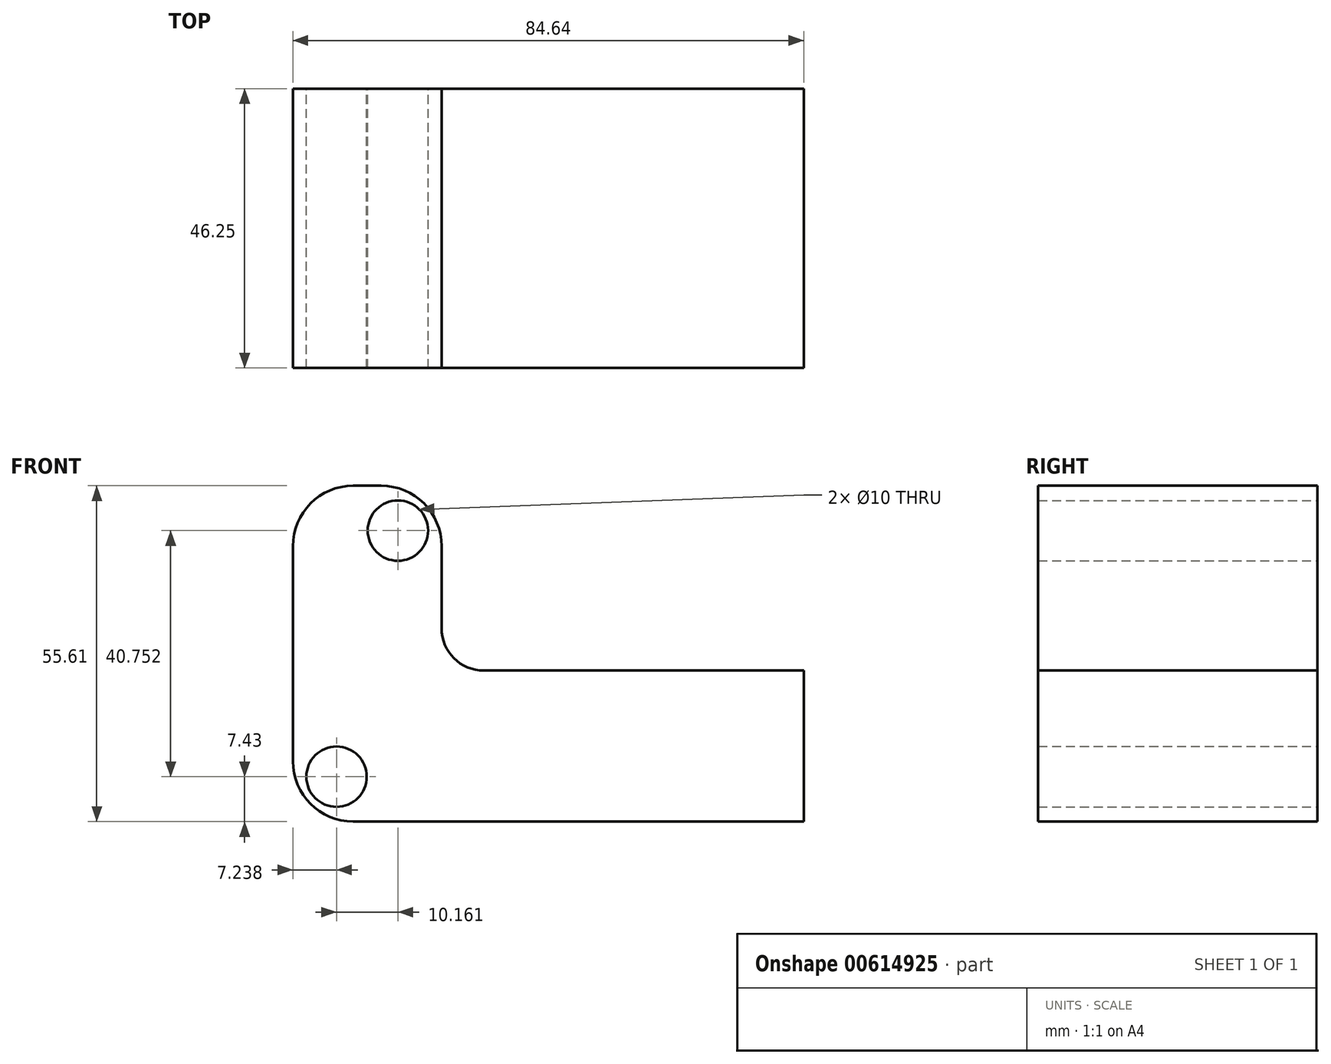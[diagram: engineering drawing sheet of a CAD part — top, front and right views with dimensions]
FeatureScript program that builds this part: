
annotation { "Feature Type Name" : "Feature", "Feature Type Description" : "" }
export const myFeature = defineFeature(function(context is Context, id is Id, definition is map)
    precondition{}
    {
        {
            var Q0;
            Q0=qCreatedBy(makeId("Front.planeOp"),FACE);
            var sketch = newSketch(context, id + "F0", { "sketchPlane" : qUnion([Q0])});
            skLineSegment(sketch, "E0", {"start": v(-6.2, -11.57) * mm, "end": v(23.8, -11.57) * mm});
            skCircle(sketch, "E1", {"center": v(23.8, -11.57) * mm, "radius": 5 * mm});
            skLineSegment(sketch, "E2", {"start": v(23.8, -11.57) * mm, "end": v(33.96, 29.18) * mm});
            skCircle(sketch, "E3", {"center": v(33.96, 29.18) * mm, "radius": 5 * mm});
            skLineSegment(sketch, "E4.bottom", {"start": v(31.2, 36.61) * mm, "end": v(26.56, 36.61) * mm});
            skLineSegment(sketch, "E4.top", {"start": v(41.2, -19) * mm, "end": v(26.56, -19) * mm});
            skLineSegment(sketch, "E4.left", {"start": v(41.2, 26.61) * mm, "end": v(41.2, -19) * mm});
            skLineSegment(sketch, "E4.right", {"start": v(16.56, 26.61) * mm, "end": v(16.56, -9) * mm});
            skPoint(sketch, "E4.middle", {"position": v(28.88, 8.8) * mm});
            skPoint(sketch, "E5.visualSharp", {"position": v(16.56, -19) * mm});
            skArc(sketch, "E5.filletArc", {"start": v(16.56, -9) * mm, "mid": v(19.49, -16.07) * mm, "end": v(26.56, -19) * mm});
            skPoint(sketch, "E6.visualSharp", {"position": v(16.56, 36.61) * mm});
            skArc(sketch, "E6.filletArc", {"start": v(26.56, 36.61) * mm, "mid": v(19.49, 33.68) * mm, "end": v(16.56, 26.61) * mm});
            skPoint(sketch, "E7.visualSharp", {"position": v(41.2, 36.61) * mm});
            skArc(sketch, "E7.filletArc", {"start": v(41.2, 26.61) * mm, "mid": v(38.27, 33.68) * mm, "end": v(31.2, 36.61) * mm});
            skLineSegment(sketch, "E8.bottom", {"start": v(41.2, -19) * mm, "end": v(101.2, -19) * mm});
            skLineSegment(sketch, "E8.top", {"start": v(41.2, 6) * mm, "end": v(101.2, 6) * mm});
            skLineSegment(sketch, "E8.left", {"start": v(41.2, -19) * mm, "end": v(41.2, 6) * mm});
            skLineSegment(sketch, "E8.right", {"start": v(101.2, -19) * mm, "end": v(101.2, 6) * mm});
            skLineSegment(sketch, "E9", {"start": v(41.2, 6) * mm, "end": v(41.2, 13) * mm});
            skLineSegment(sketch, "E10", {"start": v(41.2, 13) * mm, "end": v(41.2, 6) * mm});
            skLineSegment(sketch, "E11", {"start": v(41.2, 6) * mm, "end": v(48.2, 6) * mm});
            skArc(sketch, "E12", {"start": v(41.2, 13) * mm, "mid": v(43.25, 8.05) * mm, "end": v(48.2, 6) * mm});
            skSolve(sketch);
        }
        {
            var Q0;
            Q0 = qSketchRegion(id + "F0", true);
            extrude(context, id + "F1", {"entities" : qUnion([Q0]), "depth" : 46.25 * mm, "offsetDistance" : 25 * mm});
        }
    });
